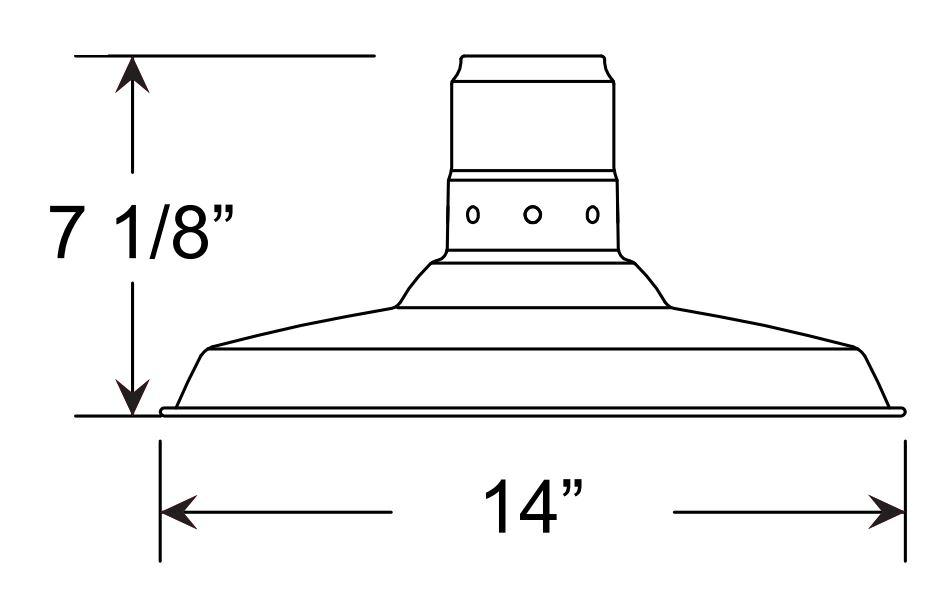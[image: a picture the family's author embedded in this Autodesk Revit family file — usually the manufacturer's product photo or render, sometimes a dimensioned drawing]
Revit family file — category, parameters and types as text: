
# Revit family: Emblem_LED
name_source: partatom
category: Lighting Fixtures
units: mm (PartAtom-declared; Revit-internal decimal feet)

## family parameters
Always vertical = Yes
Cut with Voids When Loaded = No
Light Source = Yes
OmniClass Number = 23.80.70.00
OmniClass Title = Lighting
Part Type = Normal
Room Calculation Point = No
Round Connector Dimension = Use Diameter
Shared = No
Work Plane-Based = No

## types (4) — shared parameters
Body Colour = Spun aluminium
Body Material = body
CRI = >90
Color Filter = 16777215
Construction Material = Heavy Duty spun aluminum.
Default Elevation = 0' - 0"
Description = 120-277 Voltage
Dimming = 1%
Dimming Lamp Color Temperature Shift = <None>
Efficiency = 65-125 lumens per watt
Inside body material = <By Category>
Lamp = LED
Life = L70 50,000 hours
Load Classification = Lighting
Manufacturer = ANP Lighting
Power Factor = 1
Tilt Angle = 90.00°
URL = https://www.anplighting.com
Voltage = 277 V
Warranty = 5 year limited warranty

## per-type parameters (varying)
| type | Apparent Load | Fixture Diameter | Fixture Height | M707 | M710 | M712 | M714 | Photometric Web File | Wattage Comments | Weight |
| M707 | 10 VA | 0' - 7" | 0' - 6" | Yes | No | No | No | M707M009LDNW40K.IES | 10W | 1.0 lb |
| M710 | 16 VA | 0' - 10" | 0' - 8" | No | Yes | No | No | M707M009LDNW40K.IES | 16W | 1.0 lb |
| M712 | 24 VA | 1' - 0" | 0' - 9 1/2" | No | No | Yes | No | M707M009LDNW40K.IES | 24W | 1.0 lb |
| M714 | 16 VA | 1' - 2" | 0' - 10" | No | No | No | Yes | M714M016LDNW40K.ies | 16W | 1.5 lb |

note: column(s) folded — value = type name in every type: Model

## geometry (parser evidence)
native form markers: Sweep x26
no freeform markers — native parametric forms only
